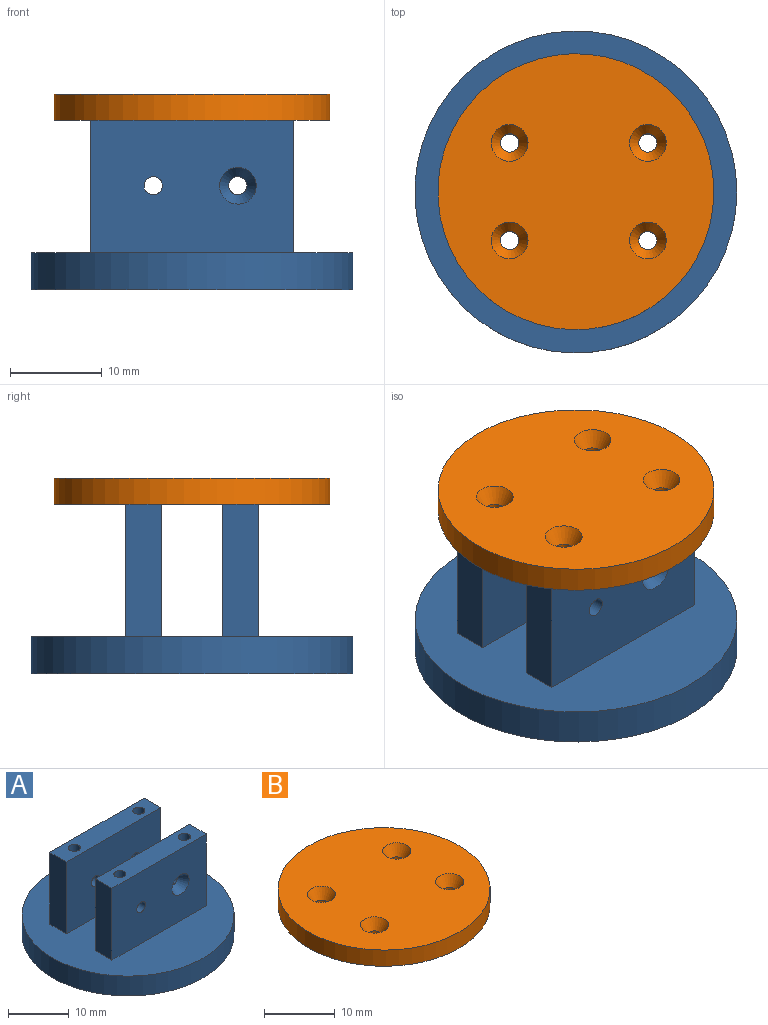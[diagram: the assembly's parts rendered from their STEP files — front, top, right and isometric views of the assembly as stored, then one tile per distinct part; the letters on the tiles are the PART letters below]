
ASSEMBLY  parts=2 mates=1
PART A: 23 faces, bbox 35x35x18.5 mm
  f0: cylinder r=17.5mm len=35mm, axis (0,0,-1), area 439.8mm2, adj f1,f2
  f1: plane 35x35mm, normal (0,0,1), area 790.5mm2, adj f0,f3,f4,f5,f6,f8,f9,f10
  f2: plane 35x35mm, normal (0,0,-1), area 949.5mm2, adj f0,f19,f20,f21,f22
  f3: plane 22x14.5mm, normal (0,1,0), area 303.3mm2, adj f1,f4,f6,f7,f15,f18
  f4: plane 14.5x3.9mm, normal (1,0,0), area 56.5mm2, adj f1,f3,f5,f7
  f5: plane 22x14.5mm, normal (0,-1,0), area 312.7mm2, adj f1,f4,f6,f7,f15,f17
  f6: plane 14.5x3.9mm, normal (-1,0,0), area 56.5mm2, adj f1,f3,f5,f7
  f7: plane 22x3.9mm, normal (0,0,1), area 79.5mm2, adj f3,f4,f5,f6,f19,f20
  f8: plane 14.5x3.9mm, normal (-1,0,0), area 56.5mm2, adj f1,f9,f10,f12
  f9: plane 22x14.5mm, normal (0,-1,0), area 303.3mm2, adj f1,f8,f11,f12,f14,f16
  f10: plane 22x14.5mm, normal (0,1,0), area 312.7mm2, adj f1,f8,f11,f12,f13,f16
  f11: plane 14.5x3.9mm, normal (1,0,0), area 56.5mm2, adj f1,f9,f10,f12
  f12: plane 22x3.9mm, normal (0,0,1), area 79.5mm2, adj f8,f9,f10,f11,f21,f22
  f13: cylinder r=1mm len=2.17mm, axis (0,-1,0), area 13.6mm2, adj f10,f14
  f14: cone r=1mm half-angle=30deg, axis (0,-1,0), area 18.8mm2, adj f9,f13
  f15: cylinder r=1mm len=3.9mm, axis (0,-1,0), area 24.5mm2, adj f3,f5
  f16: cylinder r=1mm len=3.9mm, axis (0,1,0), area 24.5mm2, adj f9,f10
  f17: cylinder r=1mm len=2.17mm, axis (0,1,0), area 13.6mm2, adj f5,f18
  f18: cone r=1mm half-angle=30deg, axis (0,1,0), area 18.8mm2, adj f3,f17
  f19: cylinder r=1mm len=18.5mm, axis (0,0,1), area 116.2mm2, adj f2,f7
  f20: cylinder r=1mm len=18.5mm, axis (0,0,1), area 116.2mm2, adj f2,f7
  f21: cylinder r=1mm len=18.5mm, axis (0,0,1), area 116.2mm2, adj f2,f12
  f22: cylinder r=1mm len=18.5mm, axis (0,0,1), area 116.2mm2, adj f2,f12
PART B: 11 faces, bbox 30x30x2.8 mm
  f0: cylinder r=15mm len=30mm, axis (0,0,-1), area 263.9mm2, adj f1,f2
  f1: plane 30x30mm, normal (0,0,1), area 656.6mm2, adj f0,f4,f6,f8,f10
  f2: plane 30x30mm, normal (0,0,-1), area 694.3mm2, adj f0,f3,f5,f7,f9
  f3: cylinder r=1mm len=2mm, axis (0,0,1), area 6.7mm2, adj f2,f4
  f4: cone r=1mm half-angle=30deg, axis (0,0,1), area 18.8mm2, adj f1,f3
  f5: cylinder r=1mm len=2mm, axis (0,0,1), area 6.7mm2, adj f2,f6
  f6: cone r=1mm half-angle=30deg, axis (0,0,1), area 18.8mm2, adj f1,f5
  f7: cylinder r=1mm len=2mm, axis (0,0,1), area 6.7mm2, adj f2,f8
  f8: cone r=1mm half-angle=30deg, axis (0,0,1), area 18.8mm2, adj f1,f7
  f9: cylinder r=1mm len=2mm, axis (0,0,1), area 6.7mm2, adj f2,f10
  f10: cone r=1mm half-angle=30deg, axis (0,0,1), area 18.8mm2, adj f1,f9
PLACE A rot(axis=(0,0,-1),0deg) t=(-5.37,5.73,4.16)mm fixed
PLACE B t=(-5.37,5.73,4.09)mm
MATE slider B.f7 <-> A.f21  axis (0,0,1) through (2.45,0.43,23.66)mm
